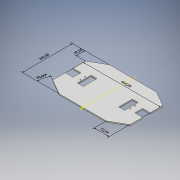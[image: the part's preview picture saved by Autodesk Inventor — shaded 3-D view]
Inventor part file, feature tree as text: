
AUTODESK INVENTOR PART (.ipt)
format: ipt  version: 2018 (Build 220112000, 112)  size: 168,448 bytes
history: native  units: mm
features: other x8, extrude x2, chamfer x2, hole x2, sketch x2, mirror x1
ambient origin geometry x8: Origin, YZ Plane, XZ Plane, XY Plane, X Axis, Y Axis, Z Axis, Center Point
bodies: Solide1 (feature_tree)
feature tree (17):
  other  "Annotations"
  extrude  "Extrusion1"  Depth=400.0mm
  chamfer  "Chanfrein1"  Distance=260.0mm
  chamfer  "Chanfrein2"  Distance=6.0mm
  extrude  "Extrusion4"  Depth=45.0mm TaperAngle=60.0deg
  other  "Point de construction1"
  other  "Plan de construction1"
  hole  "Perçage1"  [1 undecoded]
  hole  "Perçage2"  [1 undecoded]
  mirror  "Symétrie1"
  sketch  "Esquisse1"
  sketch  "Esquisse4"
  other  "Cote linéaire 1"
  other  "Cote linéaire 3"
  other  "Cote linéaire 4"
  other  "Cote angulaire 1"
  other  "Cote linéaire 5"
note: 2 required parameter values undecoded (feature->parameter linkage not recoverable at this tier; creation-order binding heuristic only, values carry confidence <= 0.55)
